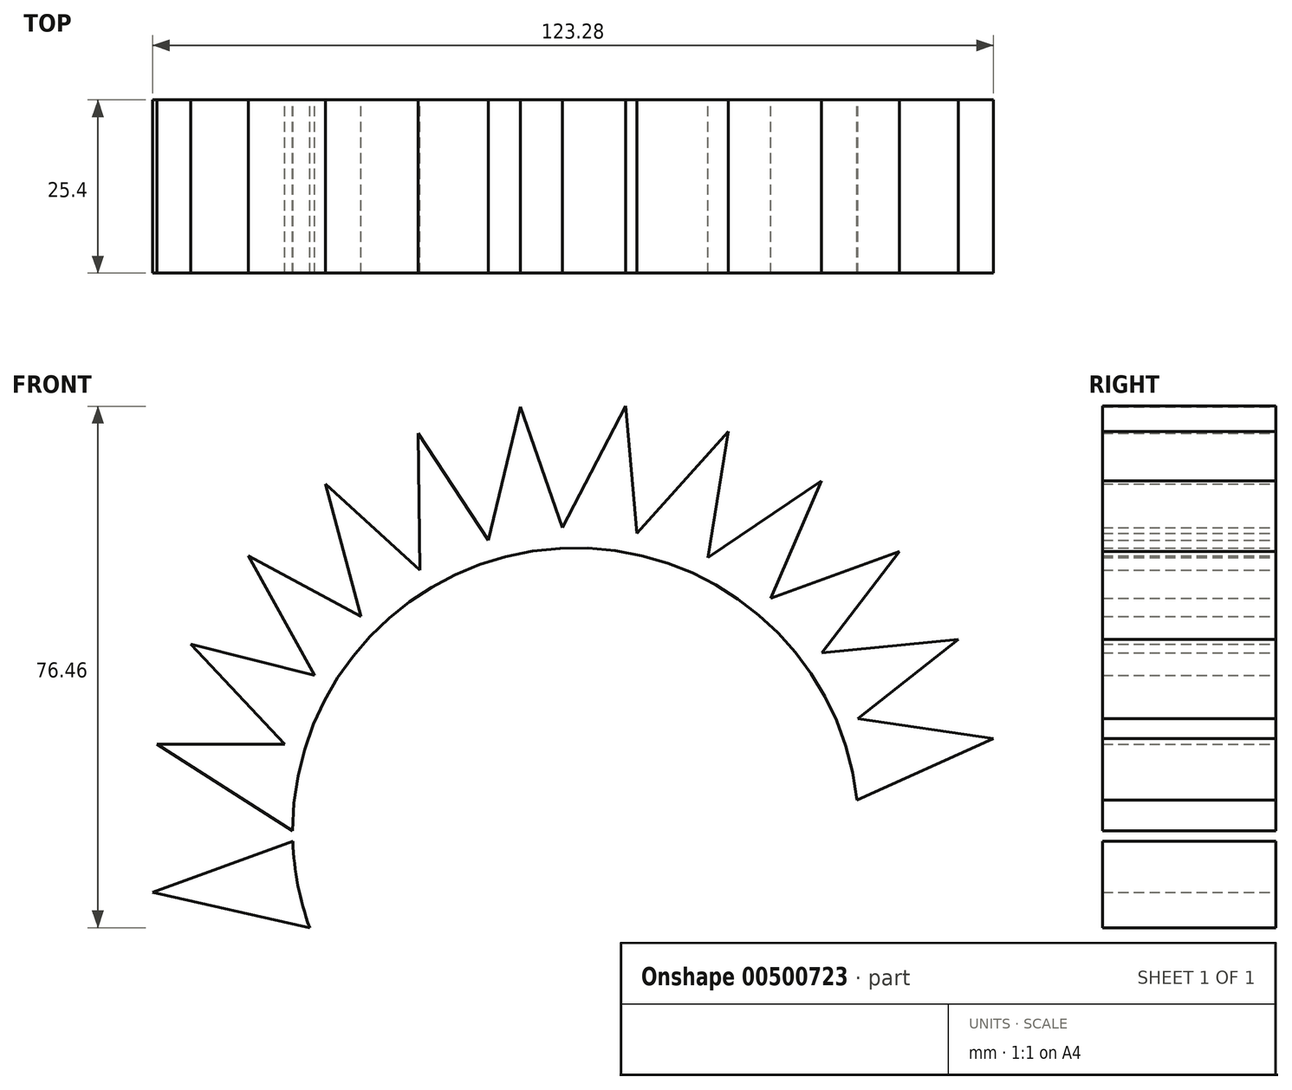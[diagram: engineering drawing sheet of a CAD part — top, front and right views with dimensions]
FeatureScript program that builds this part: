
annotation { "Feature Type Name" : "Feature", "Feature Type Description" : "" }
export const myFeature = defineFeature(function(context is Context, id is Id, definition is map)
    precondition{}
    {
        {
            var Q0;
            Q0=qCreatedBy(makeId("Front.planeOp"),FACE);
            var sketch = newSketch(context, id + "F0", { "sketchPlane" : qUnion([Q0])});
            skArc(sketch, "E0", {"start": v(41.5, 0) * mm, "mid": v(0, 41.5) * mm, "end": v(-41.5, 0) * mm});
            skLineSegment(sketch, "E1", {"start": v(-41.5, 0) * mm, "end": v(-61.4, 12.74) * mm});
            skLineSegment(sketch, "E2", {"start": v(-39.5, 12.74) * mm, "end": v(-61.4, 12.74) * mm});
            skLineSegment(sketch, "E3.1.0", {"start": v(-40.23, 10.16) * mm, "end": v(-56.41, 27.38) * mm});
            skLineSegment(sketch, "E3.1.1", {"start": v(-35.18, 22.01) * mm, "end": v(-56.41, 27.38) * mm});
            skArc(sketch, "E3.1.2", {"start": v(41.5, 0) * mm, "mid": v(5.12, 41.18) * mm, "end": v(-40.23, 10.16) * mm});
            skLineSegment(sketch, "E3.2.0", {"start": v(-36.53, 19.7) * mm, "end": v(-48, 40.35) * mm});
            skLineSegment(sketch, "E3.2.1", {"start": v(-28.72, 29.95) * mm, "end": v(-48, 40.35) * mm});
            skArc(sketch, "E3.2.2", {"start": v(41.5, 0) * mm, "mid": v(10.16, 40.23) * mm, "end": v(-36.53, 19.7) * mm});
            skLineSegment(sketch, "E3.3.0", {"start": v(-30.6, 28.03) * mm, "end": v(-36.66, 50.87) * mm});
            skLineSegment(sketch, "E3.3.1", {"start": v(-20.51, 36.07) * mm, "end": v(-36.66, 50.87) * mm});
            skArc(sketch, "E3.3.2", {"start": v(41.5, 0) * mm, "mid": v(15.04, 38.68) * mm, "end": v(-30.6, 28.03) * mm});
            skLineSegment(sketch, "E3.4.0", {"start": v(-22.8, 34.67) * mm, "end": v(-23.1, 58.3) * mm});
            skLineSegment(sketch, "E3.4.1", {"start": v(-11.06, 40) * mm, "end": v(-23.1, 58.3) * mm});
            skLineSegment(sketch, "E3.5.0", {"start": v(-13.62, 39.2) * mm, "end": v(-8.13, 62.17) * mm});
            skLineSegment(sketch, "E3.5.1", {"start": v(-0.94, 41.49) * mm, "end": v(-8.13, 62.17) * mm});
            skLineSegment(sketch, "E3.6.0", {"start": v(-3.62, 41.34) * mm, "end": v(7.34, 62.27) * mm});
            skLineSegment(sketch, "E3.6.1", {"start": v(9.25, 40.45) * mm, "end": v(7.34, 62.27) * mm});
            skLineSegment(sketch, "E3.7.0", {"start": v(6.61, 40.97) * mm, "end": v(22.35, 58.58) * mm});
            skLineSegment(sketch, "E3.7.1", {"start": v(18.87, 36.96) * mm, "end": v(22.35, 58.58) * mm});
            skLineSegment(sketch, "E3.8.0", {"start": v(16.44, 38.1) * mm, "end": v(36.01, 51.33) * mm});
            skLineSegment(sketch, "E3.8.1", {"start": v(27.34, 31.22) * mm, "end": v(36.01, 51.33) * mm});
            skLineSegment(sketch, "E3.9.0", {"start": v(25.26, 32.92) * mm, "end": v(47.48, 40.95) * mm});
            skLineSegment(sketch, "E3.9.1", {"start": v(34.15, 23.58) * mm, "end": v(47.48, 40.95) * mm});
            skLineSegment(sketch, "E3.10.0", {"start": v(32.55, 25.74) * mm, "end": v(56.06, 28.09) * mm});
            skLineSegment(sketch, "E3.10.1", {"start": v(38.88, 14.5) * mm, "end": v(56.06, 28.09) * mm});
            skLineSegment(sketch, "E3.11.0", {"start": v(37.86, 16.99) * mm, "end": v(61.23, 13.51) * mm});
            skLineSegment(sketch, "E3.11.1", {"start": v(41.25, 4.55) * mm, "end": v(61.23, 13.51) * mm});
            skLineSegment(sketch, "E3.12.0", {"start": v(40.87, 7.2) * mm, "end": v(44.13, 5.84) * mm});
            skArc(sketch, "E3.22.2", {"start": v(27.59, 31) * mm, "mid": v(-23.3, 34.33) * mm, "end": v(-39, -14.2) * mm});
            skArc(sketch, "E3.23.2", {"start": v(34.33, 23.3) * mm, "mid": v(-18.9, 36.95) * mm, "end": v(-39, -14.2) * mm});
            skLineSegment(sketch, "E3.24.0", {"start": v(-39, -14.2) * mm, "end": v(-62.05, -9.03) * mm});
            skLineSegment(sketch, "E3.24.1", {"start": v(-41.47, -1.54) * mm, "end": v(-62.05, -9.03) * mm});
            skArc(sketch, "E3.24.2", {"start": v(39, 14.2) * mm, "mid": v(-14.2, 39) * mm, "end": v(-39, -14.2) * mm});
            skLineSegment(sketch, "E3.anchor1", {"start": v(0, 0) * mm, "end": v(-61.4, 12.74) * mm, "construction": true});
            skLineSegment(sketch, "E3.anchor2", {"start": v(0, 0) * mm, "end": v(-62.05, -9.03) * mm, "construction": true});
            skPoint(sketch, "E4.orphan", {"position": v(-34.33, -23.3) * mm});
            skPoint(sketch, "E5.orphan", {"position": v(-27.59, -31) * mm});
            skPoint(sketch, "E6.orphan", {"position": v(30.6, -28.03) * mm});
            skPoint(sketch, "E7.orphan", {"position": v(36.53, -19.7) * mm});
            skPoint(sketch, "E8.orphan", {"position": v(62.67, -1.88) * mm});
            skPoint(sketch, "E9.orphan", {"position": v(40.23, -10.16) * mm});
            skSolve(sketch);
        }
        {
            var Q0;
            Q0 = qSketchRegion(id + "F0", true);
            extrude(context, id + "F1", {"entities" : qUnion([Q0]), "depth" : 25.4 * mm});
        }
    });
